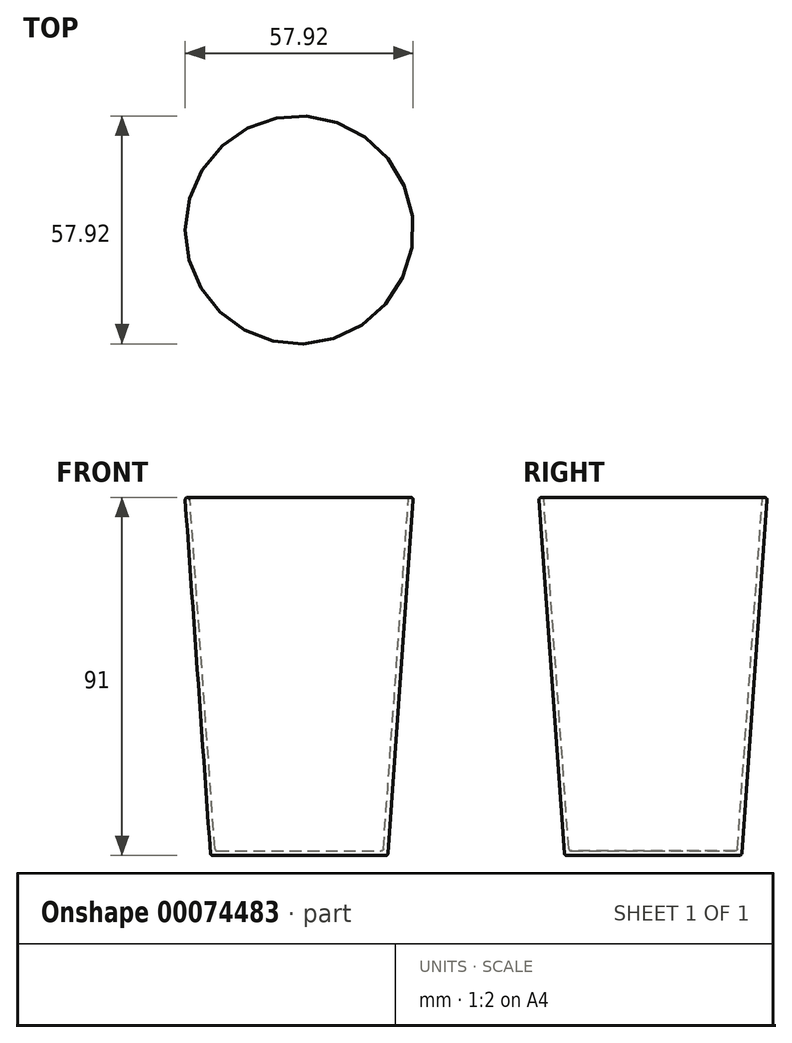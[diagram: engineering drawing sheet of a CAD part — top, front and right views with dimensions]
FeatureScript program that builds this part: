
annotation { "Feature Type Name" : "Feature", "Feature Type Description" : "" }
export const myFeature = defineFeature(function(context is Context, id is Id, definition is map)
    precondition{}
    {
        {
            var Q0;
            Q0=qCreatedBy(makeId("Front.planeOp"),FACE);
            var sketch = newSketch(context, id + "F0", { "sketchPlane" : qUnion([Q0])});
            skLineSegment(sketch, "E0", {"start": v(-29, 91) * mm, "end": v(-22.5, 0) * mm});
            skLineSegment(sketch, "E1", {"start": v(0, 0) * mm, "end": v(0, 50.67) * mm});
            skLineSegment(sketch, "E2", {"start": v(-22.5, 0) * mm, "end": v(0, 0) * mm});
            skLineSegment(sketch, "E3", {"start": v(0, 1.2) * mm, "end": v(-21.38, 1.2) * mm});
            skLineSegment(sketch, "E4", {"start": v(-21.38, 1.2) * mm, "end": v(-27.8, 91) * mm});
            skLineSegment(sketch, "E5", {"start": v(-27.8, 91) * mm, "end": v(-29, 91) * mm});
            skSolve(sketch);
        }
        {
            var Q0;
            Q0 = qSketchRegion(id + "F0", true);
            var Q1;
            Q1=sQuery(id+"F0.wireOp",EDGE,"E1");
            revolve(context, id + "F1", {"entities" : qUnion([Q0]), "axis" : qUnion([Q1]), "revolveType" : RevolveType.FULL});
        }
        {
            var Q0;
            Q0=makeQuery(id+"F1.opRevolve","SWEPT_FACE",FACE,{"disambiguationData":[OSD([sQuery(id+"F0.wireOp",EDGE,"E5")])]});
            var Q1;
            Q1=makeQuery(id+"F1.opRevolve","SWEPT_FACE",FACE,{"disambiguationData":[OSD([sQuery(id+"F0.wireOp",EDGE,"E3")])]});
            var Q2;
            Q2=makeQuery(id+"F1.opRevolve","SWEPT_FACE",FACE,{"disambiguationData":[OSD([sQuery(id+"F0.wireOp",EDGE,"E2")])]});
            fillet(context, id + "F2", {"entities" : qUnion([Q0, Q1, Q2]), "radius" : .6 * mm, "tangentPropagation" : true, "allowEdgeOverflow" : false});
        }
    });
